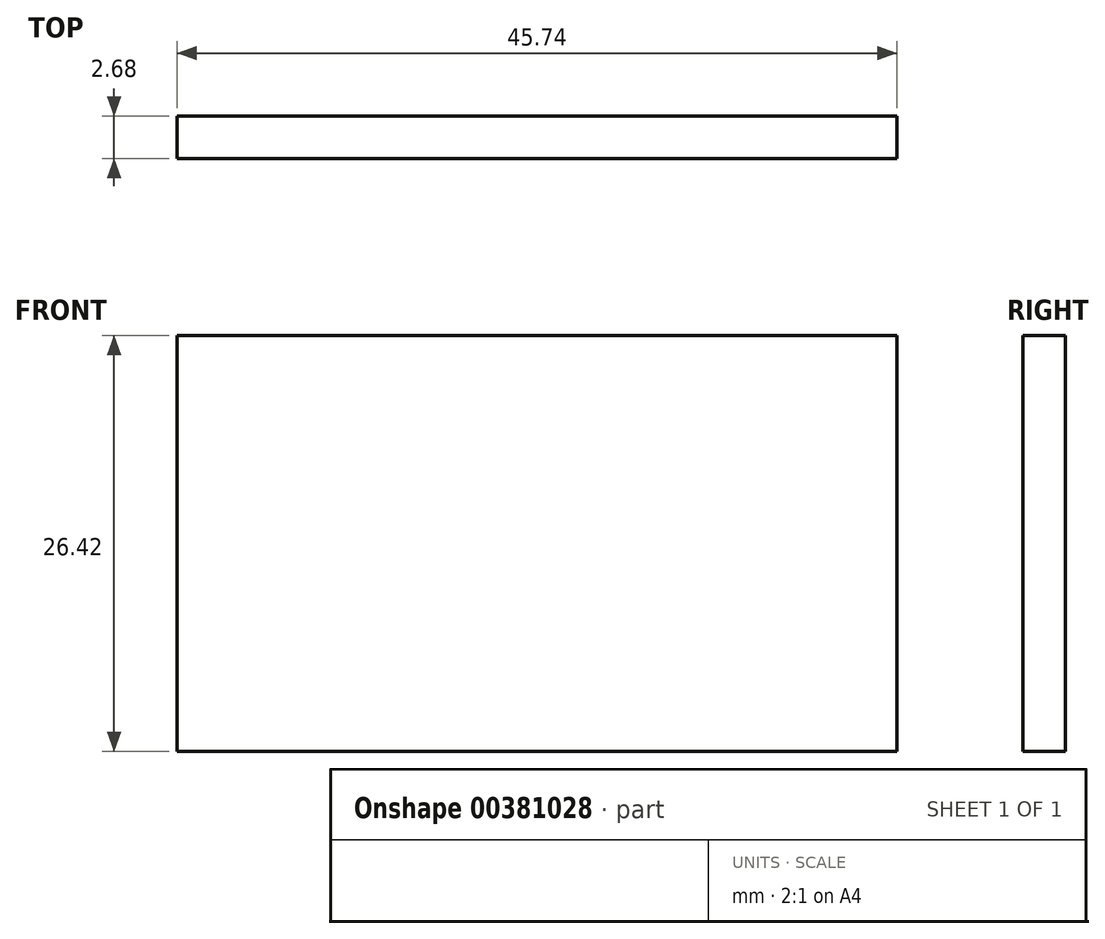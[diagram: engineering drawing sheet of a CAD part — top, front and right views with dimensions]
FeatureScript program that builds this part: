
annotation { "Feature Type Name" : "Feature", "Feature Type Description" : "" }
export const myFeature = defineFeature(function(context is Context, id is Id, definition is map)
    precondition{}
    {
        {
            var Q0;
            Q0=qCreatedBy(makeId("Front.planeOp"),FACE);
            var sketch = newSketch(context, id + "F0", { "sketchPlane" : qUnion([Q0])});
            skLineSegment(sketch, "E0.bottom", {"start": v(17.79, 3.22) * mm, "end": v(-27.95, 3.22) * mm});
            skLineSegment(sketch, "E0.top", {"start": v(17.79, 29.64) * mm, "end": v(-27.95, 29.64) * mm});
            skLineSegment(sketch, "E0.left", {"start": v(17.79, 3.22) * mm, "end": v(17.79, 29.64) * mm});
            skLineSegment(sketch, "E0.right", {"start": v(-27.95, 3.22) * mm, "end": v(-27.95, 29.64) * mm});
            skPoint(sketch, "E0.middle", {"position": v(-5.08, 16.43) * mm});
            skSolve(sketch);
        }
        {
            var Q0;
            Q0 = qSketchRegion(id + "F0", true);
            extrude(context, id + "F1", {"entities" : qUnion([Q0]), "depth" : 2.68 * mm});
        }
    });
